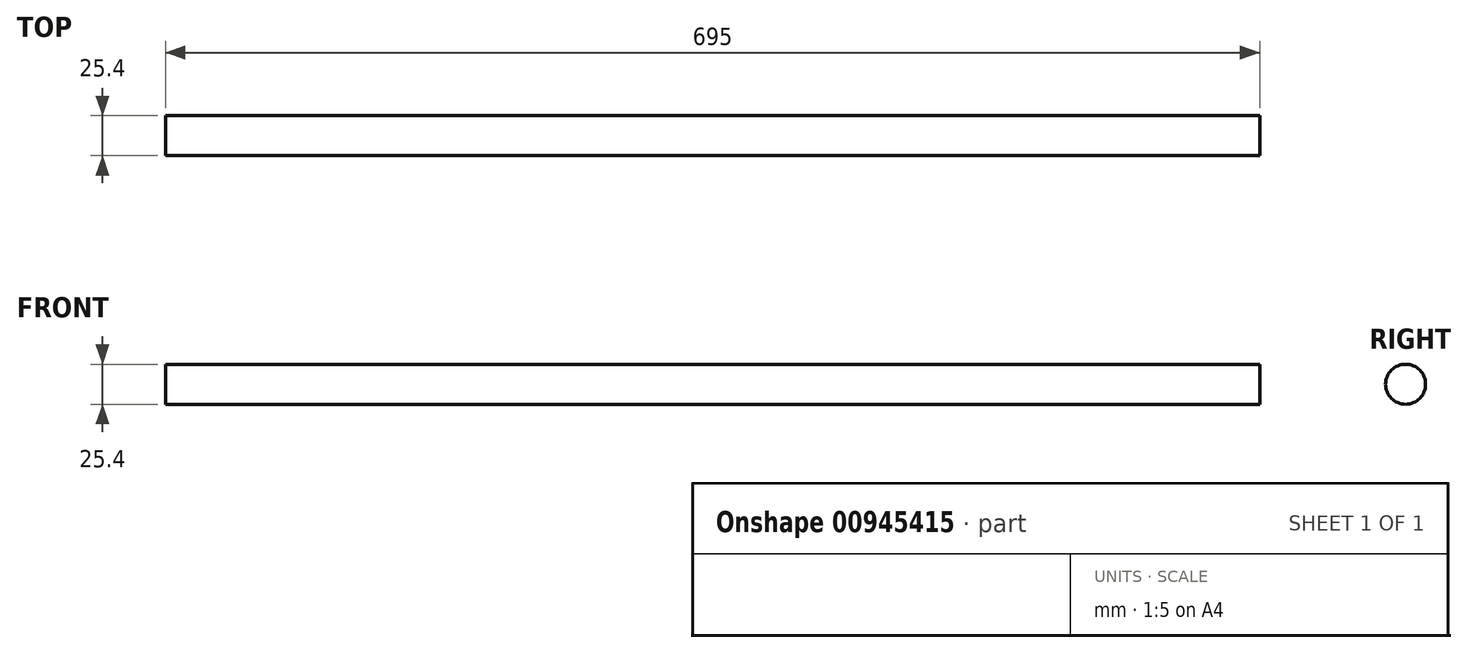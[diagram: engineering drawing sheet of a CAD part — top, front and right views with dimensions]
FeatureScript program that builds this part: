
annotation { "Feature Type Name" : "Feature", "Feature Type Description" : "" }
export const myFeature = defineFeature(function(context is Context, id is Id, definition is map)
    precondition{}
    {
        {
            var Q0;
            Q0=qCreatedBy(makeId("Right.planeOp"),FACE);
            var sketch = newSketch(context, id + "F0", { "sketchPlane" : qUnion([Q0])});
            skCircle(sketch, "E0", {"center": v(0, 0) * mm, "radius": 12.7 * mm});
            skSolve(sketch);
        }
        {
            var Q0;
            Q0=sQuery(id+"F0.wireOp",EDGE,"E0");
            extrude(context, id + "F1", {"bodyType" : ToolBodyType.SURFACE, "surfaceEntities" : qUnion([Q0]), "depth" : 695 * mm, "offsetDistance" : 25.4 * mm});
        }
    });
